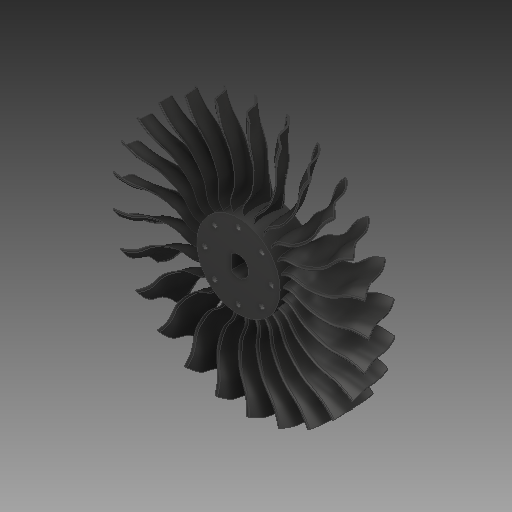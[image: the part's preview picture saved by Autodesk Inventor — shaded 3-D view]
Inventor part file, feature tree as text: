
AUTODESK INVENTOR PART (.ipt)
format: ipt  version: 2019 (Build 230136000, 136)  size: 14,802,944 bytes
history: native  units: mm
features: sketch x9, plane x7, extrude x2, pattern_circular x2, fillet x2, hole x1, thread x1, loft x1
ambient origin geometry x8: Origin, YZ Plane, XZ Plane, XY Plane, X Axis, Y Axis, Z Axis, Center Point
bodies: Solid1 (feature_tree)
feature tree (25):
  extrude  "Extrusion1"  Depth=70.0mm
  hole  "Hole1"  [1 undecoded]
  thread  "Thread2"  [1 undecoded]
  pattern_circular  "Circular Pattern1"  Count=4  [1 undecoded]
  plane  "Work Plane3"
  plane  "Work Plane8"
  sketch  "Sketch6"  dims[d5=4.0mm d6=6.0mm d7=4.0mm d8=2.0mm d9=90.0deg d10=8.0mm d11=20.594885mm d14=80.0mm d15=360.0deg]
  plane  "Work Plane4"
  sketch  "Sketch7"  dims[d17=12.0mm]
  plane  "Work Plane5"
  sketch  "Sketch8"  dims[d21=1.0mm]
  plane  "Work Plane6"
  sketch  "Sketch9"  dims[d22=2.5mm]
  plane  "Work Plane7"
  plane  "Work Plane9"
  loft  "Loft1"
  fillet  "Fillet2"  Radius=20.0mm
  fillet  "Fillet3"  Radius=5.0mm
  pattern_circular  "Circular Pattern2"  Count=2  [1 undecoded]
  extrude  "Extrusion3"  Depth=10.0mm
  sketch  "Sketch1"  dims[d0=17.0mm d1=70.0mm]
  sketch  "Sketch2"  dims[d2=30.0mm d3=0.0mm d4=28.0mm]
  sketch  "Sketch10"  dims[d23=25.0mm d24=40.0mm]
  sketch  "Sketch12"  dims[d25=20.0mm d26=1.0mm d27=20.0mm d29=5.0mm]
  sketch  "Sketch13"  dims[d30=1.0mm d31=20.0mm d32=1.0mm d33=0.0mm d34=90.0deg d35=0.0mm d36=90.0deg d37=0.0mm d38=90.0deg d39=0.0mm d40=90.0deg d41=0.0mm d42=90.0deg d45=250.0mm d46=360.0deg d50=-1.0mm d55=30.0mm d57=0.0mm d58=90.0deg d59=10.0mm d60=0.0mm d61=1.0mm d63=1.0mm d64=215.0mm d65=270.0mm d66=0.0mm d67=0.0mm d68=2.0mm d69=2.0mm]
note: 4 required parameter values undecoded (feature->parameter linkage not recoverable at this tier; creation-order binding heuristic only, values carry confidence <= 0.55)
